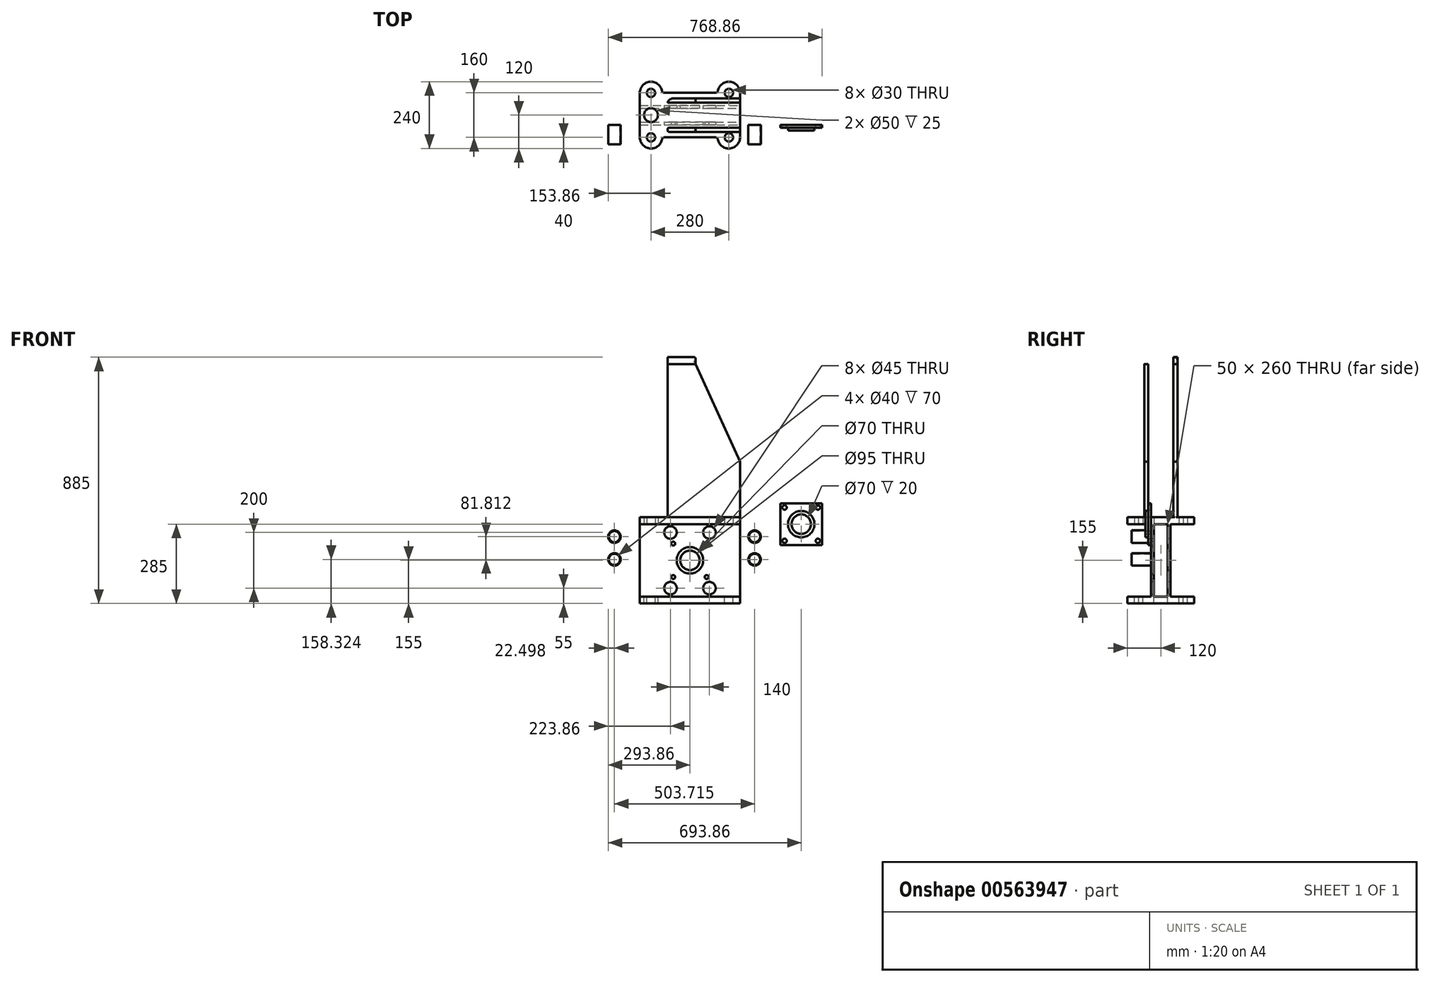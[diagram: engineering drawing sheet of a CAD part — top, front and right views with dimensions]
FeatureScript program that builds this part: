
annotation { "Feature Type Name" : "Feature", "Feature Type Description" : "" }
export const myFeature = defineFeature(function(context is Context, id is Id, definition is map)
    precondition{}
    {
        {
            var Q0;
            Q0=qCreatedBy(makeId("Top.planeOp"),FACE);
            var sketch = newSketch(context, id + "F0", { "sketchPlane" : qUnion([Q0])});
            skCircle(sketch, "E0", {"center": v(-140, 80) * mm, "radius": 40 * mm});
            skCircle(sketch, "E1", {"center": v(140, 80) * mm, "radius": 40 * mm});
            skCircle(sketch, "E2", {"center": v(-140, -80) * mm, "radius": 40 * mm});
            skCircle(sketch, "E3", {"center": v(140, -80) * mm, "radius": 40 * mm});
            skLineSegment(sketch, "E4", {"start": v(180, 80) * mm, "end": v(180, -80) * mm});
            skLineSegment(sketch, "E5", {"start": v(-180, 80) * mm, "end": v(-180, -80) * mm});
            skLineSegment(sketch, "E6", {"start": v(-100, 80) * mm, "end": v(100, 80) * mm});
            skLineSegment(sketch, "E7", {"start": v(-100, -80) * mm, "end": v(100, -80) * mm});
            skCircle(sketch, "E8", {"center": v(-140, 0) * mm, "radius": 25 * mm});
            skCircle(sketch, "E9", {"center": v(-140, 80) * mm, "radius": 15 * mm});
            skCircle(sketch, "E10", {"center": v(140, 80) * mm, "radius": 15 * mm});
            skCircle(sketch, "E11", {"center": v(-140, -80) * mm, "radius": 15 * mm});
            skCircle(sketch, "E12", {"center": v(140, -80) * mm, "radius": 15 * mm});
            skSolve(sketch);
        }
        {
            var Q0;
            {var subQ3=sQuery(id+"F0.wireOp",EDGE,"E4");Q0=makeQuery(id+"F0.imprint","IMPRINT",FACE,{"disambiguationData":[TD([[makeQuery(id+"F0.imprint","IMPRINT",EDGE,{"derivedFrom":subQ3}),-1.0]])]});}
            var Q1;
            Q1=makeQuery(id+"F0.imprint","IMPRINT",FACE,{"disambiguationData":[TD([[makeQuery(id+"F0.imprint","IMPRINT",EDGE,{"derivedFrom":sQuery(id+"F0.wireOp",EDGE,"E9")}),-1.0]])]});
            var Q2;
            Q2=makeQuery(id+"F0.imprint","IMPRINT",FACE,{"disambiguationData":[TD([[makeQuery(id+"F0.imprint","IMPRINT",EDGE,{"derivedFrom":sQuery(id+"F0.wireOp",EDGE,"E10")}),-1.0]])]});
            var Q3;
            Q3=makeQuery(id+"F0.imprint","IMPRINT",FACE,{"disambiguationData":[TD([[makeQuery(id+"F0.imprint","IMPRINT",EDGE,{"derivedFrom":sQuery(id+"F0.wireOp",EDGE,"E12")}),-1.0]])]});
            var Q4;
            Q4=makeQuery(id+"F0.imprint","IMPRINT",FACE,{"disambiguationData":[TD([[makeQuery(id+"F0.imprint","IMPRINT",EDGE,{"derivedFrom":sQuery(id+"F0.wireOp",EDGE,"E11")}),-1.0]])]});
            extrude(context, id + "F1", {"entities" : qUnion([Q0, Q1, Q2, Q3, Q4]), "depth" : 25 * mm, "offsetDistance" : 25 * mm});
        }
        {
            var Q0;
            Q0=makeQuery(id+"F1.opExtrude","SWEPT_EDGE",EDGE,{"disambiguationData":[OSD([sQuery(id+"F0.wireOp",EDGE,"E0"),sQuery(id+"F0.wireOp",EDGE,"E6")])]});
            var Q1;
            Q1=makeQuery(id+"F1.opExtrude","SWEPT_EDGE",EDGE,{"disambiguationData":[OSD([sQuery(id+"F0.wireOp",EDGE,"E1"),sQuery(id+"F0.wireOp",EDGE,"E6")])]});
            var Q2;
            Q2=makeQuery(id+"F1.opExtrude","SWEPT_EDGE",EDGE,{"disambiguationData":[OSD([sQuery(id+"F0.wireOp",EDGE,"E3"),sQuery(id+"F0.wireOp",EDGE,"E7")])]});
            var Q3;
            Q3=makeQuery(id+"F1.opExtrude","SWEPT_EDGE",EDGE,{"disambiguationData":[OSD([sQuery(id+"F0.wireOp",EDGE,"E2"),sQuery(id+"F0.wireOp",EDGE,"E7")])]});
            fillet(context, id + "F2", {"entities" : qUnion([Q0, Q1, Q2, Q3]), "radius" : 10 * mm, "tangentPropagation" : true, "allowEdgeOverflow" : false});
        }
        {
            var Q0;
            Q0=makeQuery(id+"F1.opExtrude","CAP_FACE",FACE,{"disambiguationData":[OSD([sQuery(id+"F0.wireOp",EDGE,"E0"),sQuery(id+"F0.wireOp",EDGE,"E1"),sQuery(id+"F0.wireOp",EDGE,"E2"),sQuery(id+"F0.wireOp",EDGE,"E3"),sQuery(id+"F0.wireOp",EDGE,"E4"),sQuery(id+"F0.wireOp",EDGE,"E5"),sQuery(id+"F0.wireOp",EDGE,"E6"),sQuery(id+"F0.wireOp",EDGE,"E7"),sQuery(id+"F0.wireOp",EDGE,"E8"),sQuery(id+"F0.wireOp",EDGE,"E9"),sQuery(id+"F0.wireOp",EDGE,"E10"),sQuery(id+"F0.wireOp",EDGE,"E11"),sQuery(id+"F0.wireOp",EDGE,"E12")])],"isStart":true});
            var sketch = newSketch(context, id + "F3", { "sketchPlane" : qUnion([Q0])});
            skLineSegment(sketch, "E13.bottom", {"start": v(-180, 25) * mm, "end": v(180, 25) * mm});
            skLineSegment(sketch, "E13.top", {"start": v(-180, 35) * mm, "end": v(180, 35) * mm});
            skLineSegment(sketch, "E13.left", {"start": v(-180, 25) * mm, "end": v(-180, 35) * mm});
            skLineSegment(sketch, "E13.right", {"start": v(180, 25) * mm, "end": v(180, 35) * mm});
            skLineSegment(sketch, "E14.bottom", {"start": v(-180, -25) * mm, "end": v(180, -25) * mm});
            skLineSegment(sketch, "E14.top", {"start": v(-180, -35) * mm, "end": v(180, -35) * mm});
            skLineSegment(sketch, "E14.left", {"start": v(-180, -25) * mm, "end": v(-180, -35) * mm});
            skLineSegment(sketch, "E14.right", {"start": v(180, -25) * mm, "end": v(180, -35) * mm});
            skSolve(sketch);
        }
        {
            var Q0;
            Q0=makeQuery(id+"F3.imprint","IMPRINT",FACE,{"disambiguationData":[TD([[makeQuery(id+"F3.imprint","IMPRINT",EDGE,{"derivedFrom":sQuery(id+"F3.wireOp",EDGE,"E13.top")}),-1.0]])]});
            var Q1;
            Q1=makeQuery(id+"F3.imprint","IMPRINT",FACE,{"disambiguationData":[TD([[makeQuery(id+"F3.imprint","IMPRINT",EDGE,{"derivedFrom":sQuery(id+"F3.wireOp",EDGE,"E14.top")}),1.0]])]});
            extrude(context, id + "F4", {"entities" : qUnion([Q0, Q1]), "operationType" : NewBodyOperationType.ADD, "depth" : 260 * mm, "offsetDistance" : 25 * mm});
        }
        {
            var Q0;
            Q0=makeQuery(id+"F4.opExtrude","CAP_FACE",FACE,{"disambiguationData":[OSD([sQuery(id+"F3.wireOp",EDGE,"E13.bottom"),sQuery(id+"F3.wireOp",EDGE,"E13.top"),sQuery(id+"F3.wireOp",EDGE,"E13.left"),sQuery(id+"F3.wireOp",EDGE,"E13.right")])],"isStart":false});
            var sketch = newSketch(context, id + "F5", { "sketchPlane" : qUnion([Q0])});
            skLineSegment(sketch, "E15.0", {"start": v(-180, 35) * mm, "end": v(-180, 80) * mm});
            skArc(sketch, "E16.0", {"start": v(-180, 80) * mm, "mid": v(-144.02, 119.8) * mm, "end": v(-100.8, 88) * mm});
            skLineSegment(sketch, "E17.0", {"start": v(-91.01, 80) * mm, "end": v(91.01, 80) * mm});
            skLineSegment(sketch, "E18.0.0", {"start": v(-180, 80) * mm, "end": v(-180, 35) * mm});
            skLineSegment(sketch, "E18.0.1", {"start": v(-180, 35) * mm, "end": v(180, 35) * mm});
            skLineSegment(sketch, "E18.0.2", {"start": v(180, 35) * mm, "end": v(180, 80) * mm});
            skArc(sketch, "E18.0.3", {"start": v(180, 80) * mm, "mid": v(144.02, 119.8) * mm, "end": v(100.8, 88) * mm});
            skArc(sketch, "E18.0.4", {"start": v(100.8, 88) * mm, "mid": v(97.33, 82.25) * mm, "end": v(91.01, 80) * mm});
            skLineSegment(sketch, "E18.0.5", {"start": v(91.01, 80) * mm, "end": v(-91.01, 80) * mm});
            skArc(sketch, "E18.0.6", {"start": v(-91.01, 80) * mm, "mid": v(-97.33, 82.25) * mm, "end": v(-100.8, 88) * mm});
            skArc(sketch, "E18.0.7", {"start": v(-100.8, 88) * mm, "mid": v(-144.02, 119.8) * mm, "end": v(-180, 80) * mm});
            skLineSegment(sketch, "E19.0.0", {"start": v(180, -35) * mm, "end": v(-180, -35) * mm});
            skLineSegment(sketch, "E19.0.1", {"start": v(-180, -35) * mm, "end": v(-180, -80) * mm});
            skArc(sketch, "E19.0.2", {"start": v(-180, -80) * mm, "mid": v(-144.02, -119.8) * mm, "end": v(-100.8, -88) * mm});
            skArc(sketch, "E19.0.3", {"start": v(-100.8, -88) * mm, "mid": v(-97.33, -82.25) * mm, "end": v(-91.01, -80) * mm});
            skLineSegment(sketch, "E19.0.4", {"start": v(-91.01, -80) * mm, "end": v(91.01, -80) * mm});
            skArc(sketch, "E19.0.5", {"start": v(91.01, -80) * mm, "mid": v(97.33, -82.25) * mm, "end": v(100.8, -88) * mm});
            skArc(sketch, "E19.0.6", {"start": v(100.8, -88) * mm, "mid": v(144.02, -119.8) * mm, "end": v(180, -80) * mm});
            skLineSegment(sketch, "E19.0.7", {"start": v(180, -80) * mm, "end": v(180, -35) * mm});
            skArc(sketch, "E20.0.0", {"start": v(-140, 25) * mm, "mid": v(-115, 0) * mm, "end": v(-140, -25) * mm});
            skLineSegment(sketch, "E20.0.1", {"start": v(-140, -25) * mm, "end": v(180, -25) * mm});
            skLineSegment(sketch, "E20.0.2", {"start": v(180, -25) * mm, "end": v(180, 25) * mm});
            skLineSegment(sketch, "E20.0.3", {"start": v(180, 25) * mm, "end": v(-140, 25) * mm});
            skLineSegment(sketch, "E21.0.0", {"start": v(-180, 25) * mm, "end": v(-180, -25) * mm});
            skLineSegment(sketch, "E21.0.1", {"start": v(-180, -25) * mm, "end": v(-140, -25) * mm});
            skArc(sketch, "E21.0.2", {"start": v(-140, -25) * mm, "mid": v(-165, 0) * mm, "end": v(-140, 25) * mm});
            skLineSegment(sketch, "E21.0.3", {"start": v(-140, 25) * mm, "end": v(-180, 25) * mm});
            skLineSegment(sketch, "E22.0.0", {"start": v(180, 35) * mm, "end": v(-180, 35) * mm});
            skLineSegment(sketch, "E22.0.1", {"start": v(-180, 35) * mm, "end": v(-180, 25) * mm});
            skLineSegment(sketch, "E22.0.2", {"start": v(-180, 25) * mm, "end": v(180, 25) * mm});
            skLineSegment(sketch, "E22.0.3", {"start": v(180, 25) * mm, "end": v(180, 35) * mm});
            skLineSegment(sketch, "E23.0.0", {"start": v(-180, -25) * mm, "end": v(-180, -35) * mm});
            skLineSegment(sketch, "E23.0.1", {"start": v(-180, -35) * mm, "end": v(180, -35) * mm});
            skLineSegment(sketch, "E23.0.2", {"start": v(180, -35) * mm, "end": v(180, -25) * mm});
            skLineSegment(sketch, "E23.0.3", {"start": v(180, -25) * mm, "end": v(-180, -25) * mm});
            skCircle(sketch, "E24", {"center": v(-140, 80) * mm, "radius": 15 * mm});
            skCircle(sketch, "E25", {"center": v(140, 80) * mm, "radius": 15 * mm});
            skCircle(sketch, "E26", {"center": v(140, -80) * mm, "radius": 15 * mm});
            skCircle(sketch, "E27", {"center": v(-140, -80) * mm, "radius": 15 * mm});
            skSolve(sketch);
        }
        {
            var Q0;
            Q0=qSketchRegion(id+"F5",true);
            extrude(context, id + "F6", {"entities" : qUnion([Q0]), "operationType" : NewBodyOperationType.ADD, "depth" : 25 * mm, "offsetDistance" : 25 * mm});
        }
        {
            var Q0;
            Q0=makeQuery(id+"F4.opExtrude","SWEPT_FACE",FACE,{"disambiguationData":[OSD([sQuery(id+"F3.wireOp",EDGE,"E13.top")])]});
            var sketch = newSketch(context, id + "F7", { "sketchPlane" : qUnion([Q0])});
            skLineSegment(sketch, "E28", {"start": v(0, 0) * mm, "end": v(0, -293.43) * mm, "construction": true});
            skPoint(sketch, "E28.endSnap0", {"position": v(0, -260) * mm});
            skCircle(sketch, "E29", {"center": v(-70, -30) * mm, "radius": 22.5 * mm});
            skCircle(sketch, "E30", {"center": v(70, -30) * mm, "radius": 22.5 * mm});
            skCircle(sketch, "E31", {"center": v(-70, -230) * mm, "radius": 22.5 * mm});
            skCircle(sketch, "E32", {"center": v(70, -230) * mm, "radius": 22.5 * mm});
            skCircle(sketch, "E33", {"center": v(0, -130) * mm, "radius": 35 * mm});
            skSolve(sketch);
        }
        {
            var Q0;
            Q0=makeQuery(id+"F7.imprint","IMPRINT",FACE,{"disambiguationData":[TD([[makeQuery(id+"F7.imprint","IMPRINT",EDGE,{"derivedFrom":sQuery(id+"F7.wireOp",EDGE,"E29")}),1.0]])]});
            var Q1;
            Q1=makeQuery(id+"F7.imprint","IMPRINT",FACE,{"disambiguationData":[TD([[makeQuery(id+"F7.imprint","IMPRINT",EDGE,{"derivedFrom":sQuery(id+"F7.wireOp",EDGE,"E30")}),1.0]])]});
            var Q2;
            Q2=makeQuery(id+"F7.imprint","IMPRINT",FACE,{"disambiguationData":[TD([[makeQuery(id+"F7.imprint","IMPRINT",EDGE,{"derivedFrom":sQuery(id+"F7.wireOp",EDGE,"E32")}),1.0]])]});
            var Q3;
            Q3=makeQuery(id+"F7.imprint","IMPRINT",FACE,{"disambiguationData":[TD([[makeQuery(id+"F7.imprint","IMPRINT",EDGE,{"derivedFrom":sQuery(id+"F7.wireOp",EDGE,"E31")}),1.0]])]});
            extrude(context, id + "F8", {"entities" : qUnion([Q0, Q1, Q2, Q3]), "operationType" : NewBodyOperationType.REMOVE, "oppositeDirection" : true, "depth" : 70 * mm, "offsetDistance" : 25 * mm});
        }
        {
            var Q0;
            Q0=makeQuery(id+"F4.opExtrude","SWEPT_FACE",FACE,{"disambiguationData":[OSD([sQuery(id+"F3.wireOp",EDGE,"E13.top")])]});
            var sketch = newSketch(context, id + "F9", { "sketchPlane" : qUnion([Q0])});
            skCircle(sketch, "E34", {"center": v(-271.36, -44.86) * mm, "radius": 22.5 * mm});
            skCircle(sketch, "E35", {"center": v(-271.36, -44.86) * mm, "radius": 20 * mm});
            skCircle(sketch, "E36", {"center": v(-271.36, -126.68) * mm, "radius": 22.5 * mm});
            skCircle(sketch, "E37", {"center": v(-271.36, -126.68) * mm, "radius": 20 * mm});
            skCircle(sketch, "E38", {"center": v(232.35, -44.86) * mm, "radius": 22.5 * mm});
            skCircle(sketch, "E39", {"center": v(232.35, -44.86) * mm, "radius": 20 * mm});
            skCircle(sketch, "E40", {"center": v(232.35, -126.68) * mm, "radius": 22.5 * mm});
            skCircle(sketch, "E41", {"center": v(232.35, -126.68) * mm, "radius": 20 * mm});
            skSolve(sketch);
        }
        {
            var Q0;
            Q0=makeQuery(id+"F9.imprint","IMPRINT",FACE,{"disambiguationData":[TD([[makeQuery(id+"F9.imprint","IMPRINT",EDGE,{"derivedFrom":sQuery(id+"F9.wireOp",EDGE,"E34")}),1.0]])]});
            var Q1;
            Q1=makeQuery(id+"F9.imprint","IMPRINT",FACE,{"disambiguationData":[TD([[makeQuery(id+"F9.imprint","IMPRINT",EDGE,{"derivedFrom":sQuery(id+"F9.wireOp",EDGE,"E36")}),1.0]])]});
            var Q2;
            Q2=makeQuery(id+"F9.imprint","IMPRINT",FACE,{"disambiguationData":[TD([[makeQuery(id+"F9.imprint","IMPRINT",EDGE,{"derivedFrom":sQuery(id+"F9.wireOp",EDGE,"E38")}),1.0]])]});
            var Q3;
            Q3=makeQuery(id+"F9.imprint","IMPRINT",FACE,{"disambiguationData":[TD([[makeQuery(id+"F9.imprint","IMPRINT",EDGE,{"derivedFrom":sQuery(id+"F9.wireOp",EDGE,"E40")}),1.0]])]});
            extrude(context, id + "F10", {"entities" : qUnion([Q0, Q1, Q2, Q3]), "depth" : 70 * mm, "offsetDistance" : 25 * mm});
        }
        {
            var Q0;
            Q0=makeQuery(id+"F1.opExtrude","CAP_FACE",FACE,{"disambiguationData":[OSD([sQuery(id+"F0.wireOp",EDGE,"E0"),sQuery(id+"F0.wireOp",EDGE,"E1"),sQuery(id+"F0.wireOp",EDGE,"E2"),sQuery(id+"F0.wireOp",EDGE,"E3"),sQuery(id+"F0.wireOp",EDGE,"E4"),sQuery(id+"F0.wireOp",EDGE,"E5"),sQuery(id+"F0.wireOp",EDGE,"E6"),sQuery(id+"F0.wireOp",EDGE,"E7"),sQuery(id+"F0.wireOp",EDGE,"E8"),sQuery(id+"F0.wireOp",EDGE,"E9"),sQuery(id+"F0.wireOp",EDGE,"E10"),sQuery(id+"F0.wireOp",EDGE,"E11"),sQuery(id+"F0.wireOp",EDGE,"E12")])],"isStart":false});
            var sketch = newSketch(context, id + "F11", { "sketchPlane" : qUnion([Q0])});
            skLineSegment(sketch, "E42.bottom", {"start": v(180, 60) * mm, "end": v(-80, 60) * mm});
            skLineSegment(sketch, "E42.top", {"start": v(180, 45) * mm, "end": v(-80, 45) * mm});
            skLineSegment(sketch, "E42.left", {"start": v(180, 60) * mm, "end": v(180, 45) * mm});
            skLineSegment(sketch, "E42.right", {"start": v(-80, 60) * mm, "end": v(-80, 45) * mm});
            skLineSegment(sketch, "E43.bottom", {"start": v(180, -60) * mm, "end": v(-80, -60) * mm});
            skLineSegment(sketch, "E43.top", {"start": v(180, -45) * mm, "end": v(-80, -45) * mm});
            skLineSegment(sketch, "E43.left", {"start": v(180, -60) * mm, "end": v(180, -45) * mm});
            skLineSegment(sketch, "E43.right", {"start": v(-80, -60) * mm, "end": v(-80, -45) * mm});
            skSolve(sketch);
        }
        {
            var Q0;
            Q0=makeQuery(id+"F11.imprint","IMPRINT",FACE,{"disambiguationData":[TD([[makeQuery(id+"F11.imprint","IMPRINT",EDGE,{"derivedFrom":sQuery(id+"F11.wireOp",EDGE,"E42.bottom")}),1.0]])]});
            var Q1;
            Q1=makeQuery(id+"F11.imprint","IMPRINT",FACE,{"disambiguationData":[TD([[makeQuery(id+"F11.imprint","IMPRINT",EDGE,{"derivedFrom":sQuery(id+"F11.wireOp",EDGE,"E43.bottom")}),-1.0]])]});
            extrude(context, id + "F12", {"entities" : qUnion([Q0, Q1]), "operationType" : NewBodyOperationType.ADD, "depth" : 550 * mm, "offsetDistance" : 25 * mm});
        }
        {
            var Q0;
            Q0=makeQuery(id+"F12.opExtrude","SWEPT_FACE",FACE,{"disambiguationData":[OSD([sQuery(id+"F11.wireOp",EDGE,"E43.bottom")])]});
            var sketch = newSketch(context, id + "F13", { "sketchPlane" : qUnion([Q0])});
            skLineSegment(sketch, "E44", {"start": v(20, 575) * mm, "end": v(180, 225) * mm});
            skSolve(sketch);
        }
        {
            var Q0;
            {var subQ0=sQuery(id+"F13.wireOp",EDGE,"E44");Q0=makeQuery(id+"F13.imprint","IMPRINT",FACE,{"disambiguationData":[TD([[makeQuery(id+"F13.imprint","IMPRINT",EDGE,{"derivedFrom":subQ0}),1.0]])]});}
            extrude(context, id + "F14", {"entities" : qUnion([Q0]), "operationType" : NewBodyOperationType.REMOVE, "endBound" : BoundingType.SYMMETRIC, "depth" : 70 * mm, "offsetDistance" : 25 * mm});
        }
        {
            var Q0;
            Q0=makeQuery(id+"F12.opExtrude","SWEPT_FACE",FACE,{"disambiguationData":[OSD([sQuery(id+"F11.wireOp",EDGE,"E42.bottom")])]});
            var sketch = newSketch(context, id + "F15", { "sketchPlane" : qUnion([Q0])});
            skLineSegment(sketch, "E45", {"start": v(-20, 575) * mm, "end": v(-180, 225) * mm});
            skSolve(sketch);
        }
        {
            var Q0;
            {var subQ0=sQuery(id+"F15.wireOp",EDGE,"E45");Q0=makeQuery(id+"F15.imprint","IMPRINT",FACE,{"disambiguationData":[TD([[makeQuery(id+"F15.imprint","IMPRINT",EDGE,{"derivedFrom":subQ0}),-1.0]])]});}
            extrude(context, id + "F16", {"entities" : qUnion([Q0]), "operationType" : NewBodyOperationType.REMOVE, "oppositeDirection" : true, "depth" : 70 * mm, "offsetDistance" : 25 * mm});
        }
        {
            var Q0;
            Q0=makeQuery(id+"F12.opExtrude","CAP_FACE",FACE,{"disambiguationData":[OSD([sQuery(id+"F11.wireOp",EDGE,"E42.bottom"),sQuery(id+"F11.wireOp",EDGE,"E42.top"),sQuery(id+"F11.wireOp",EDGE,"E42.left"),sQuery(id+"F11.wireOp",EDGE,"E42.right")])],"isStart":false});
            var sketch = newSketch(context, id + "F17", { "sketchPlane" : qUnion([Q0])});
            skLineSegment(sketch, "E46.1.0", {"start": v(-80, -60) * mm, "end": v(20, -60) * mm});
            skLineSegment(sketch, "E46.1.1", {"start": v(20, -60) * mm, "end": v(20, -45) * mm});
            skLineSegment(sketch, "E46.1.2", {"start": v(20, -45) * mm, "end": v(-80, -45) * mm});
            skLineSegment(sketch, "E46.1.3", {"start": v(-80, -45) * mm, "end": v(-80, -60) * mm});
            skLineSegment(sketch, "E46.2.0", {"start": v(180, -80) * mm, "end": v(180, -60) * mm});
            skLineSegment(sketch, "E46.2.1", {"start": v(180, -60) * mm, "end": v(-80, -60) * mm});
            skLineSegment(sketch, "E46.2.2", {"start": v(-80, -60) * mm, "end": v(-80, -45) * mm});
            skLineSegment(sketch, "E46.2.3", {"start": v(-80, -45) * mm, "end": v(180, -45) * mm});
            skLineSegment(sketch, "E46.2.4", {"start": v(180, -45) * mm, "end": v(180, 45) * mm});
            skLineSegment(sketch, "E46.2.5", {"start": v(180, 45) * mm, "end": v(-80, 45) * mm});
            skLineSegment(sketch, "E46.2.6", {"start": v(-80, 45) * mm, "end": v(-80, 60) * mm});
            skLineSegment(sketch, "E46.2.7", {"start": v(-80, 60) * mm, "end": v(180, 60) * mm});
            skLineSegment(sketch, "E46.2.8", {"start": v(180, 60) * mm, "end": v(180, 80) * mm});
            skArc(sketch, "E46.2.9", {"start": v(180, 80) * mm, "mid": v(144.02, 119.8) * mm, "end": v(100.8, 88) * mm});
            skArc(sketch, "E46.2.10", {"start": v(100.8, 88) * mm, "mid": v(97.33, 82.25) * mm, "end": v(91.01, 80) * mm});
            skLineSegment(sketch, "E46.2.11", {"start": v(91.01, 80) * mm, "end": v(-91.01, 80) * mm});
            skArc(sketch, "E46.2.12", {"start": v(-91.01, 80) * mm, "mid": v(-97.33, 82.25) * mm, "end": v(-100.8, 88) * mm});
            skArc(sketch, "E46.2.13", {"start": v(-100.8, 88) * mm, "mid": v(-144.02, 119.8) * mm, "end": v(-180, 80) * mm});
            skLineSegment(sketch, "E46.2.14", {"start": v(-180, 80) * mm, "end": v(-180, -80) * mm});
            skArc(sketch, "E46.2.15", {"start": v(-180, -80) * mm, "mid": v(-144.02, -119.8) * mm, "end": v(-100.8, -88) * mm});
            skArc(sketch, "E46.2.16", {"start": v(-100.8, -88) * mm, "mid": v(-97.33, -82.25) * mm, "end": v(-91.01, -80) * mm});
            skLineSegment(sketch, "E46.2.17", {"start": v(-91.01, -80) * mm, "end": v(91.01, -80) * mm});
            skArc(sketch, "E46.2.18", {"start": v(91.01, -80) * mm, "mid": v(97.33, -82.25) * mm, "end": v(100.8, -88) * mm});
            skArc(sketch, "E46.2.19", {"start": v(100.8, -88) * mm, "mid": v(144.02, -119.8) * mm, "end": v(180, -80) * mm});
            skLineSegment(sketch, "E47", {"start": v(20, 60) * mm, "end": v(-180, 60) * mm});
            skLineSegment(sketch, "E48", {"start": v(-180, 60) * mm, "end": v(-180, -60) * mm});
            skLineSegment(sketch, "E49", {"start": v(-180, -60) * mm, "end": v(20, -60) * mm});
            skLineSegment(sketch, "E50", {"start": v(20, 60) * mm, "end": v(20, -60) * mm});
            skCircle(sketch, "E51", {"center": v(-140, 0) * mm, "radius": 25 * mm});
            skSolve(sketch);
        }
        {
            var Q0;
            {var subQ2=sQuery(id+"F17.wireOp",EDGE,"E46.2.2");Q0=makeQuery(id+"F17.imprint","IMPRINT",FACE,{"disambiguationData":[TD([[makeQuery(id+"F17.imprint","IMPRINT",EDGE,{"derivedFrom":subQ2}),1.0]])]});}
            var Q1;
            {var subQ0=sQuery(id+"F17.wireOp",EDGE,"E46.2.6");Q1=makeQuery(id+"F17.imprint","IMPRINT",FACE,{"disambiguationData":[TD([[makeQuery(id+"F17.imprint","IMPRINT",EDGE,{"derivedFrom":subQ0}),1.0]])]});}
            var Q2;
            {var subQ0=sQuery(id+"F17.wireOp",EDGE,"E46.2.2");Q2=makeQuery(id+"F17.imprint","IMPRINT",FACE,{"disambiguationData":[TD([[makeQuery(id+"F17.imprint","IMPRINT",EDGE,{"derivedFrom":subQ0}),-1.0]])]});}
            extrude(context, id + "F18", {"entities" : qUnion([Q0, Q1, Q2]), "operationType" : NewBodyOperationType.ADD, "depth" : 25 * mm, "offsetDistance" : 25 * mm});
        }
        {
            var Q0;
            Q0=makeQuery(id+"F18.opExtrude","SWEPT_EDGE",EDGE,{"disambiguationData":[OSD([sQuery(id+"F17.wireOp",EDGE,"E46.2.14"),sQuery(id+"F17.wireOp",EDGE,"E47"),sQuery(id+"F17.wireOp",EDGE,"E48")])]});
            var Q1;
            Q1=makeQuery(id+"F18.opExtrude","SWEPT_EDGE",EDGE,{"disambiguationData":[OSD([sQuery(id+"F17.wireOp",EDGE,"E46.2.14"),sQuery(id+"F17.wireOp",EDGE,"E48"),sQuery(id+"F17.wireOp",EDGE,"E49")])]});
            fillet(context, id + "F19", {"entities" : qUnion([Q0, Q1]), "radius" : 20 * mm, "tangentPropagation" : true, "allowEdgeOverflow" : false});
        }
        {
            var Q0;
            Q0=makeQuery(id+"F18.opExtrude","CAP_EDGE",EDGE,{"disambiguationData":[OSD([sQuery(id+"F17.wireOp",EDGE,"E50")])],"isStart":false});
            var Q1;
            Q1=makeQuery(id+"F18.opExtrude","SWEPT_EDGE",EDGE,{"disambiguationData":[OSD([sQuery(id+"F17.wireOp",EDGE,"E46.2.1"),sQuery(id+"F17.wireOp",EDGE,"E49"),sQuery(id+"F17.wireOp",EDGE,"E50")])]});
            var Q2;
            Q2=makeQuery(id+"F18.opExtrude","SWEPT_EDGE",EDGE,{"disambiguationData":[OSD([sQuery(id+"F17.wireOp",EDGE,"E46.2.7"),sQuery(id+"F17.wireOp",EDGE,"E47"),sQuery(id+"F17.wireOp",EDGE,"E50")])]});
            var Q3;
            Q3=makeQuery(id+"F16.boolean.opBoolean","COPY",EDGE,{"derivedFrom":makeQuery(id+"F16.opExtrude","CAP_EDGE",EDGE,{"disambiguationData":[OSD([sQuery(id+"F15.wireOp",EDGE,"E45")])],"isStart":true})});
            var Q4;
            Q4=makeQuery(id+"F16.boolean.opBoolean","INTERSECT",EDGE,{"derivedFrom":[makeQuery(id+"F12.opExtrude","SWEPT_FACE",FACE,{"disambiguationData":[OSD([sQuery(id+"F11.wireOp",EDGE,"E42.top")])]}),makeQuery(id+"F16.opExtrude","SWEPT_FACE",FACE,{"disambiguationData":[OSD([sQuery(id+"F15.wireOp",EDGE,"E45")])]})]});
            var Q5;
            Q5=makeQuery(id+"F12.opExtrude","SWEPT_EDGE",EDGE,{"disambiguationData":[OSD([sQuery(id+"F0.wireOp",EDGE,"E4"),sQuery(id+"F11.wireOp",EDGE,"E42.top"),sQuery(id+"F11.wireOp",EDGE,"E42.left")])]});
            var Q6;
            Q6=makeQuery(id+"F12.opExtrude","SWEPT_EDGE",EDGE,{"disambiguationData":[OSD([sQuery(id+"F0.wireOp",EDGE,"E4"),sQuery(id+"F11.wireOp",EDGE,"E42.bottom"),sQuery(id+"F11.wireOp",EDGE,"E42.left")])]});
            var Q7;
            Q7=makeQuery(id+"F12.opExtrude","SWEPT_EDGE",EDGE,{"disambiguationData":[OSD([sQuery(id+"F11.wireOp",EDGE,"E42.bottom"),sQuery(id+"F11.wireOp",EDGE,"E42.right")])]});
            var Q8;
            Q8=makeQuery(id+"F12.opExtrude","SWEPT_EDGE",EDGE,{"disambiguationData":[OSD([sQuery(id+"F11.wireOp",EDGE,"E42.top"),sQuery(id+"F11.wireOp",EDGE,"E42.right")])]});
            var Q9;
            Q9=makeQuery(id+"F12.opExtrude","SWEPT_EDGE",EDGE,{"disambiguationData":[OSD([sQuery(id+"F11.wireOp",EDGE,"E43.bottom"),sQuery(id+"F11.wireOp",EDGE,"E43.right")])]});
            var Q10;
            Q10=makeQuery(id+"F12.opExtrude","SWEPT_EDGE",EDGE,{"disambiguationData":[OSD([sQuery(id+"F11.wireOp",EDGE,"E43.top"),sQuery(id+"F11.wireOp",EDGE,"E43.right")])]});
            var Q11;
            Q11=makeQuery(id+"F18.opExtrude","CAP_EDGE",EDGE,{"disambiguationData":[OSD([sQuery(id+"F17.wireOp",EDGE,"E48")])],"isStart":false});
            var Q12;
            Q12=makeQuery(id+"F18.opExtrude","CAP_EDGE",EDGE,{"disambiguationData":[OSD([sQuery(id+"F17.wireOp",EDGE,"E48")])],"isStart":true});
            var Q13;
            Q13=makeQuery(id+"F14.boolean.opBoolean","INTERSECT",EDGE,{"derivedFrom":[makeQuery(id+"F12.opExtrude","SWEPT_FACE",FACE,{"disambiguationData":[OSD([sQuery(id+"F11.wireOp",EDGE,"E43.bottom")])]}),makeQuery(id+"F14.opExtrude","SWEPT_FACE",FACE,{"disambiguationData":[OSD([sQuery(id+"F13.wireOp",EDGE,"E44")])]})]});
            var Q14;
            Q14=makeQuery(id+"F12.opExtrude","SWEPT_EDGE",EDGE,{"disambiguationData":[OSD([sQuery(id+"F0.wireOp",EDGE,"E4"),sQuery(id+"F11.wireOp",EDGE,"E43.bottom"),sQuery(id+"F11.wireOp",EDGE,"E43.left")])]});
            var Q15;
            Q15=makeQuery(id+"F12.opExtrude","SWEPT_EDGE",EDGE,{"disambiguationData":[OSD([sQuery(id+"F0.wireOp",EDGE,"E4"),sQuery(id+"F11.wireOp",EDGE,"E43.top"),sQuery(id+"F11.wireOp",EDGE,"E43.left")])]});
            var Q16;
            Q16=makeQuery(id+"F14.boolean.opBoolean","INTERSECT",EDGE,{"derivedFrom":[makeQuery(id+"F12.opExtrude","SWEPT_FACE",FACE,{"disambiguationData":[OSD([sQuery(id+"F11.wireOp",EDGE,"E43.top")])]}),makeQuery(id+"F14.opExtrude","SWEPT_FACE",FACE,{"disambiguationData":[OSD([sQuery(id+"F13.wireOp",EDGE,"E44")])]})]});
            fillet(context, id + "F20", {"entities" : qUnion([Q0, Q1, Q2, Q3, Q4, Q5, Q6, Q7, Q8, Q9, Q10, Q11, Q12, Q13, Q14, Q15, Q16]), "radius" : 5 * mm, "tangentPropagation" : true, "allowEdgeOverflow" : false});
        }
        {
            var Q0;
            Q0=makeQuery(id+"F4.opExtrude","SWEPT_FACE",FACE,{"disambiguationData":[OSD([sQuery(id+"F3.wireOp",EDGE,"E14.top")])]});
            var sketch = newSketch(context, id + "F21", { "sketchPlane" : qUnion([Q0])});
            skCircle(sketch, "E52", {"center": v(0, -130) * mm, "radius": 35 * mm});
            skSolve(sketch);
        }
        {
            var Q0;
            Q0=makeQuery(id+"F21.imprint","IMPRINT",FACE,{"disambiguationData":[TD([[makeQuery(id+"F21.imprint","IMPRINT",EDGE,{"derivedFrom":sQuery(id+"F21.wireOp",EDGE,"E52")}),1.0]])]});
            extrude(context, id + "F22", {"entities" : qUnion([Q0]), "operationType" : NewBodyOperationType.REMOVE, "oppositeDirection" : true, "depth" : 10 * mm, "offsetDistance" : 25 * mm});
        }
        {
            var Q0;
            Q0=makeQuery(id+"F4.opExtrude","SWEPT_FACE",FACE,{"disambiguationData":[OSD([sQuery(id+"F3.wireOp",EDGE,"E13.top")])]});
            var sketch = newSketch(context, id + "F23", { "sketchPlane" : qUnion([Q0])});
            skCircle(sketch, "E53", {"center": v(0, -130) * mm, "radius": 47.5 * mm});
            skCircle(sketch, "E54", {"center": v(-60, -70) * mm, "radius": 7 * mm});
            skCircle(sketch, "E55", {"center": v(60, -70) * mm, "radius": 7 * mm});
            skCircle(sketch, "E56", {"center": v(60, -190) * mm, "radius": 7 * mm});
            skCircle(sketch, "E57", {"center": v(-60, -190) * mm, "radius": 7 * mm});
            skSolve(sketch);
        }
        {
            var Q0;
            Q0=makeQuery(id+"F23.imprint","IMPRINT",FACE,{"disambiguationData":[TD([[makeQuery(id+"F23.imprint","IMPRINT",EDGE,{"derivedFrom":sQuery(id+"F23.wireOp",EDGE,"E54")}),1.0]])]});
            var Q1;
            Q1=makeQuery(id+"F23.imprint","IMPRINT",FACE,{"disambiguationData":[TD([[makeQuery(id+"F23.imprint","IMPRINT",EDGE,{"derivedFrom":sQuery(id+"F23.wireOp",EDGE,"E55")}),1.0]])]});
            var Q2;
            Q2=makeQuery(id+"F23.imprint","IMPRINT",FACE,{"disambiguationData":[TD([[makeQuery(id+"F23.imprint","IMPRINT",EDGE,{"derivedFrom":sQuery(id+"F23.wireOp",EDGE,"E53")}),1.0]])]});
            var Q3;
            Q3=makeQuery(id+"F23.imprint","IMPRINT",FACE,{"disambiguationData":[TD([[makeQuery(id+"F23.imprint","IMPRINT",EDGE,{"derivedFrom":sQuery(id+"F23.wireOp",EDGE,"E57")}),1.0]])]});
            var Q4;
            Q4=makeQuery(id+"F23.imprint","IMPRINT",FACE,{"disambiguationData":[TD([[makeQuery(id+"F23.imprint","IMPRINT",EDGE,{"derivedFrom":sQuery(id+"F23.wireOp",EDGE,"E56")}),1.0]])]});
            extrude(context, id + "F24", {"entities" : qUnion([Q0, Q1, Q2, Q3, Q4]), "operationType" : NewBodyOperationType.REMOVE, "oppositeDirection" : true, "depth" : 10 * mm, "offsetDistance" : 25 * mm});
        }
        {
            var Q0;
            Q0=makeQuery(id+"F4.opExtrude","SWEPT_FACE",FACE,{"disambiguationData":[OSD([sQuery(id+"F3.wireOp",EDGE,"E13.top")])]});
            var sketch = newSketch(context, id + "F25", { "sketchPlane" : qUnion([Q0])});
            skLineSegment(sketch, "E58.bottom", {"start": v(475, -75) * mm, "end": v(325, -75) * mm});
            skLineSegment(sketch, "E58.top", {"start": v(475, 75) * mm, "end": v(325, 75) * mm});
            skLineSegment(sketch, "E58.left", {"start": v(475, -75) * mm, "end": v(475, 75) * mm});
            skLineSegment(sketch, "E58.right", {"start": v(325, -75) * mm, "end": v(325, 75) * mm});
            skPoint(sketch, "E58.middle", {"position": v(400, 0) * mm});
            skLineSegment(sketch, "E59.bottom", {"start": v(460, -60) * mm, "end": v(340, -60) * mm, "construction": true});
            skLineSegment(sketch, "E59.top", {"start": v(460, 60) * mm, "end": v(340, 60) * mm, "construction": true});
            skLineSegment(sketch, "E59.left", {"start": v(460, -60) * mm, "end": v(460, 60) * mm, "construction": true});
            skLineSegment(sketch, "E59.right", {"start": v(340, -60) * mm, "end": v(340, 60) * mm, "construction": true});
            skCircle(sketch, "E60", {"center": v(340, 60) * mm, "radius": 8 * mm});
            skCircle(sketch, "E61", {"center": v(460, 60) * mm, "radius": 8 * mm});
            skCircle(sketch, "E62", {"center": v(340, -60) * mm, "radius": 8 * mm});
            skCircle(sketch, "E63", {"center": v(460, -60) * mm, "radius": 8 * mm});
            skCircle(sketch, "E64", {"center": v(400, 0) * mm, "radius": 35 * mm});
            skCircle(sketch, "E65", {"center": v(400, 0) * mm, "radius": 47.5 * mm});
            skSolve(sketch);
        }
        {
            var Q0;
            Q0=makeQuery(id+"F25.imprint","IMPRINT",FACE,{"disambiguationData":[TD([[makeQuery(id+"F25.imprint","IMPRINT",EDGE,{"derivedFrom":sQuery(id+"F25.wireOp",EDGE,"E58.bottom")}),-1.0]])]});
            var Q1;
            Q1=makeQuery(id+"F25.imprint","IMPRINT",FACE,{"disambiguationData":[TD([[makeQuery(id+"F25.imprint","IMPRINT",EDGE,{"derivedFrom":sQuery(id+"F25.wireOp",EDGE,"E64")}),-1.0]])]});
            extrude(context, id + "F26", {"entities" : qUnion([Q0, Q1]), "depth" : 10 * mm, "offsetDistance" : 25 * mm});
        }
        {
            var Q0;
            Q0=makeQuery(id+"F26.opExtrude","CAP_FACE",FACE,{"disambiguationData":[OSD([sQuery(id+"F25.wireOp",EDGE,"E58.bottom"),sQuery(id+"F25.wireOp",EDGE,"E58.top"),sQuery(id+"F25.wireOp",EDGE,"E58.left"),sQuery(id+"F25.wireOp",EDGE,"E58.right"),sQuery(id+"F25.wireOp",EDGE,"E60"),sQuery(id+"F25.wireOp",EDGE,"E61"),sQuery(id+"F25.wireOp",EDGE,"E62"),sQuery(id+"F25.wireOp",EDGE,"E63"),sQuery(id+"F25.wireOp",EDGE,"E64")])],"isStart":false});
            var sketch = newSketch(context, id + "F27", { "sketchPlane" : qUnion([Q0])});
            skCircle(sketch, "E66", {"center": v(400, 0) * mm, "radius": 47.5 * mm});
            skCircle(sketch, "E67", {"center": v(400, 0) * mm, "radius": 35 * mm});
            skSolve(sketch);
        }
        {
            var Q0;
            Q0=makeQuery(id+"F27.imprint","IMPRINT",FACE,{"disambiguationData":[TD([[makeQuery(id+"F27.imprint","IMPRINT",EDGE,{"derivedFrom":sQuery(id+"F27.wireOp",EDGE,"E66")}),1.0]])]});
            extrude(context, id + "F28", {"entities" : qUnion([Q0]), "operationType" : NewBodyOperationType.ADD, "depth" : 10 * mm, "offsetDistance" : 25 * mm});
        }
    });
